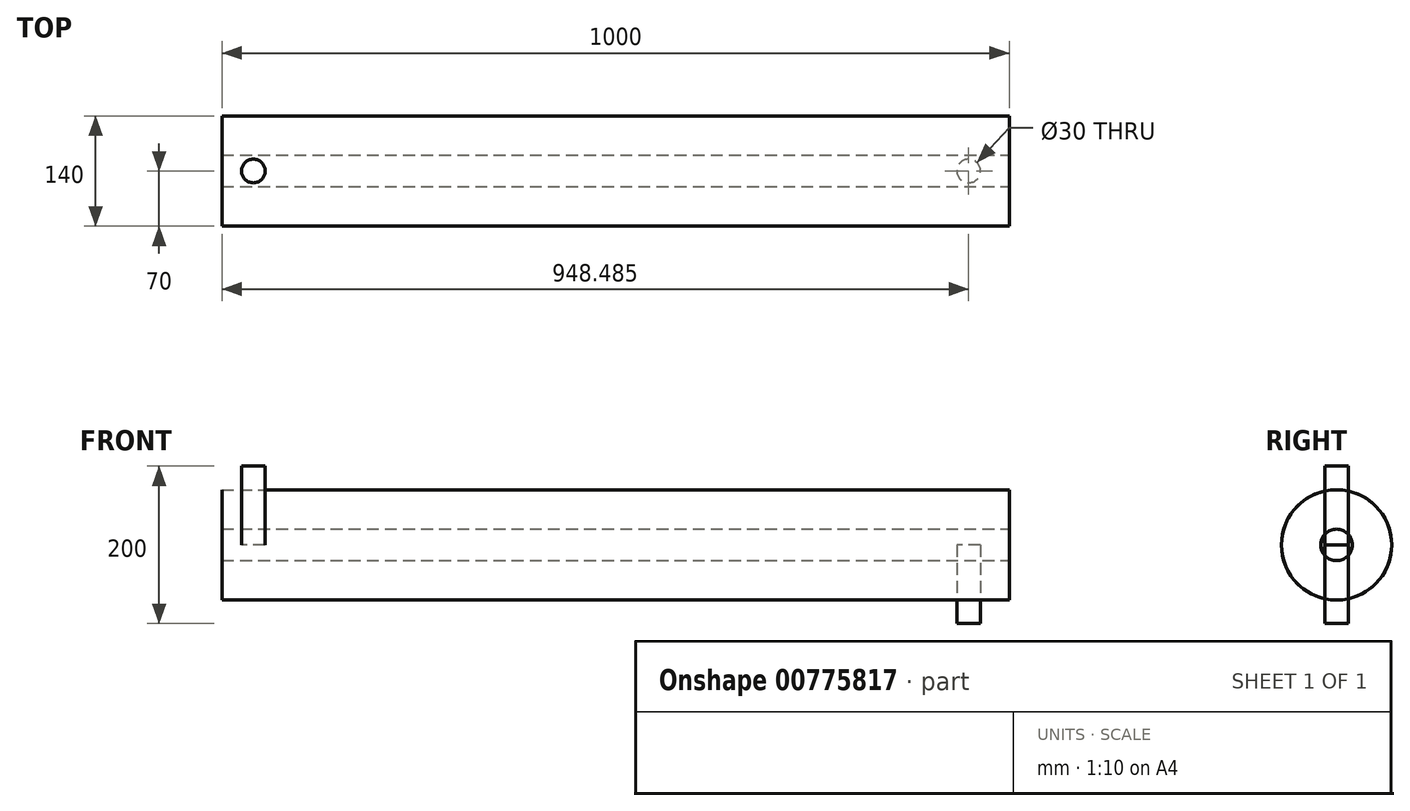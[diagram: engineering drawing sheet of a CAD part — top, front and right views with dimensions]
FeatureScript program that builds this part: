
annotation { "Feature Type Name" : "Feature", "Feature Type Description" : "" }
export const myFeature = defineFeature(function(context is Context, id is Id, definition is map)
    precondition{}
    {
        {
            var Q0;
            Q0=qCreatedBy(makeId("Right.planeOp"),FACE);
            var sketch = newSketch(context, id + "F0", { "sketchPlane" : qUnion([Q0])});
            skCircle(sketch, "E0", {"center": v(0, 0) * mm, "radius": 20 * mm});
            skSolve(sketch);
        }
        {
            var Q0;
            Q0=qCreatedBy(makeId("Right.planeOp"),FACE);
            var sketch = newSketch(context, id + "F1", { "sketchPlane" : qUnion([Q0])});
            skCircle(sketch, "E1", {"center": v(0, 0) * mm, "radius": 70 * mm});
            skSolve(sketch);
        }
        {
            var Q0;
            Q0=sQuery(id+"F1.wireOp",EDGE,"E1");
            var Q1;
            Q1=sQuery(id+"F0.wireOp",EDGE,"E0");
            extrude(context, id + "F2", {"bodyType" : ToolBodyType.SURFACE, "surfaceEntities" : qUnion([Q0, Q1]), "depth" : 1000 * mm, "offsetDistance" : 25 * mm});
        }
        {
            var Q0;
            Q0=qCreatedBy(makeId("Top.planeOp"),FACE);
            var sketch = newSketch(context, id + "F3", { "sketchPlane" : qUnion([Q0])});
            skCircle(sketch, "E2", {"center": v(39.84, 0) * mm, "radius": 15 * mm});
            skSolve(sketch);
        }
        {
            var Q0;
            Q0=sQuery(id+"F3.wireOp",EDGE,"E2");
            extrude(context, id + "F4", {"bodyType" : ToolBodyType.SURFACE, "surfaceEntities" : qUnion([Q0]), "depth" : 100 * mm, "offsetDistance" : 25 * mm});
        }
        {
            var Q0;
            Q0=qCreatedBy(makeId("Top.planeOp"),FACE);
            var sketch = newSketch(context, id + "F5", { "sketchPlane" : qUnion([Q0])});
            skCircle(sketch, "E3", {"center": v(948.48, 0) * mm, "radius": 15 * mm});
            skSolve(sketch);
        }
        {
            var Q0;
            Q0=sQuery(id+"F5.wireOp",EDGE,"E3");
            extrude(context, id + "F6", {"bodyType" : ToolBodyType.SURFACE, "surfaceEntities" : qUnion([Q0]), "oppositeDirection" : true, "depth" : 100 * mm, "offsetDistance" : 25 * mm});
        }
    });
